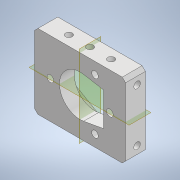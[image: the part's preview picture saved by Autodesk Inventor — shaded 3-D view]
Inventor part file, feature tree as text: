
AUTODESK INVENTOR PART (.ipt)
format: ipt  version: 2022 (Build 260153000, 153)  size: 201,728 bytes
history: native  units: mm
features: hole x4, sketch x3, extrude x2, plane x2, mirror x1, chamfer x1, thicken_offset x1, projected_geometry x1
ambient origin geometry x8: Origin, YZ Plane, XZ Plane, XY Plane, X Axis, Y Axis, Z Axis, Center Point
bodies: Solid1 (feature_tree)
feature tree (15):
  sketch  "Sketch1"  dims[d0=24.5mm d1=45.0mm]
  extrude  "Extrusion1"  Depth=45.0mm
  extrude  "Extrusion2"  Depth=55.0mm
  hole  "Hole1"  [1 undecoded]
  plane  "Work Plane1"
  hole  "Hole2"  [1 undecoded]
  hole  "Hole3"  [1 undecoded]
  plane  "Work Plane2"
  mirror  "Mirror2"
  chamfer  "Chamfer1"  Distance=2.0mm
  hole  "Hole4"  [1 undecoded]
  thicken_offset  "Thicken1"
  sketch  "Sketch3"  dims[d2=55.0mm d3=14.0mm]
  sketch  "Sketch4"  dims[d4=12.0mm d5=0.0mm d7=16.0mm d9=6.0mm d10=3.0mm d11=0.0mm d12=4.0mm d13=6.0mm d14=6.3mm d15=2.0mm d16=90.0deg d17=8.0mm d18=20.594885mm d24=4.0mm d25=6.0mm d26=4.0mm d27=2.0mm d28=90.0deg d29=8.0mm d30=20.594885mm d31=2.0mm d32=2.0mm d33=2.0mm d35=12.75mm d36=12.75mm d37=12.75mm d38=4.0mm d39=6.0mm d40=4.0mm d41=2.0mm d42=90.0deg d43=5.0mm d44=0.0mm d45=2.0mm d46=2.0mm d47=45.0deg d48=4.0mm d49=6.0mm d50=6.3mm d51=2.0mm d52=90.0deg d53=8.0mm d54=0.0mm d55=0.2mm d56=0.2mm d57=13.962634mm]
  projected_geometry  "Projected Loop1"
note: 4 required parameter values undecoded (feature->parameter linkage not recoverable at this tier; creation-order binding heuristic only, values carry confidence <= 0.55)
